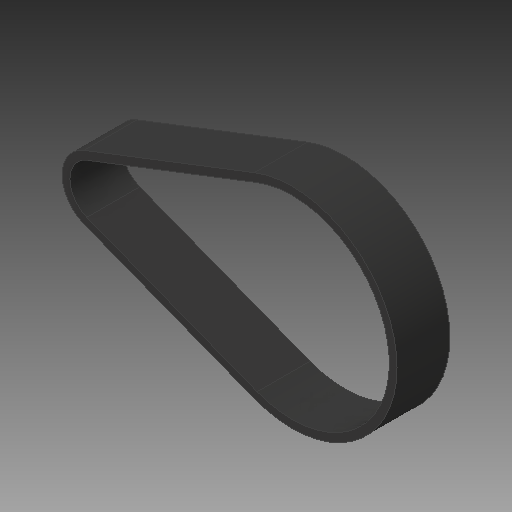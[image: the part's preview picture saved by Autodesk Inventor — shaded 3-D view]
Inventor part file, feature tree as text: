
AUTODESK INVENTOR PART (.ipt)
format: ipt  version: 2019.3 (Build 233278000, 278)  size: 120,832 bytes
history: native  units: mm
features: extrude x1, sketch x1
ambient origin geometry x8: Origin, YZ Plane, XZ Plane, XY Plane, X Axis, Y Axis, Z Axis, Center Point
bodies: Solid1 (feature_tree)
feature tree (2):
  extrude  "Extrusion1"  Depth=55.6mm
  sketch  "Sketch1"  dims[d0=16.434mm d1=55.6mm d3=1.5mm d4=56.54mm d5=0.7mm d6=0.7mm d7=1.5mm d8=15.0mm d9=0.0mm]
